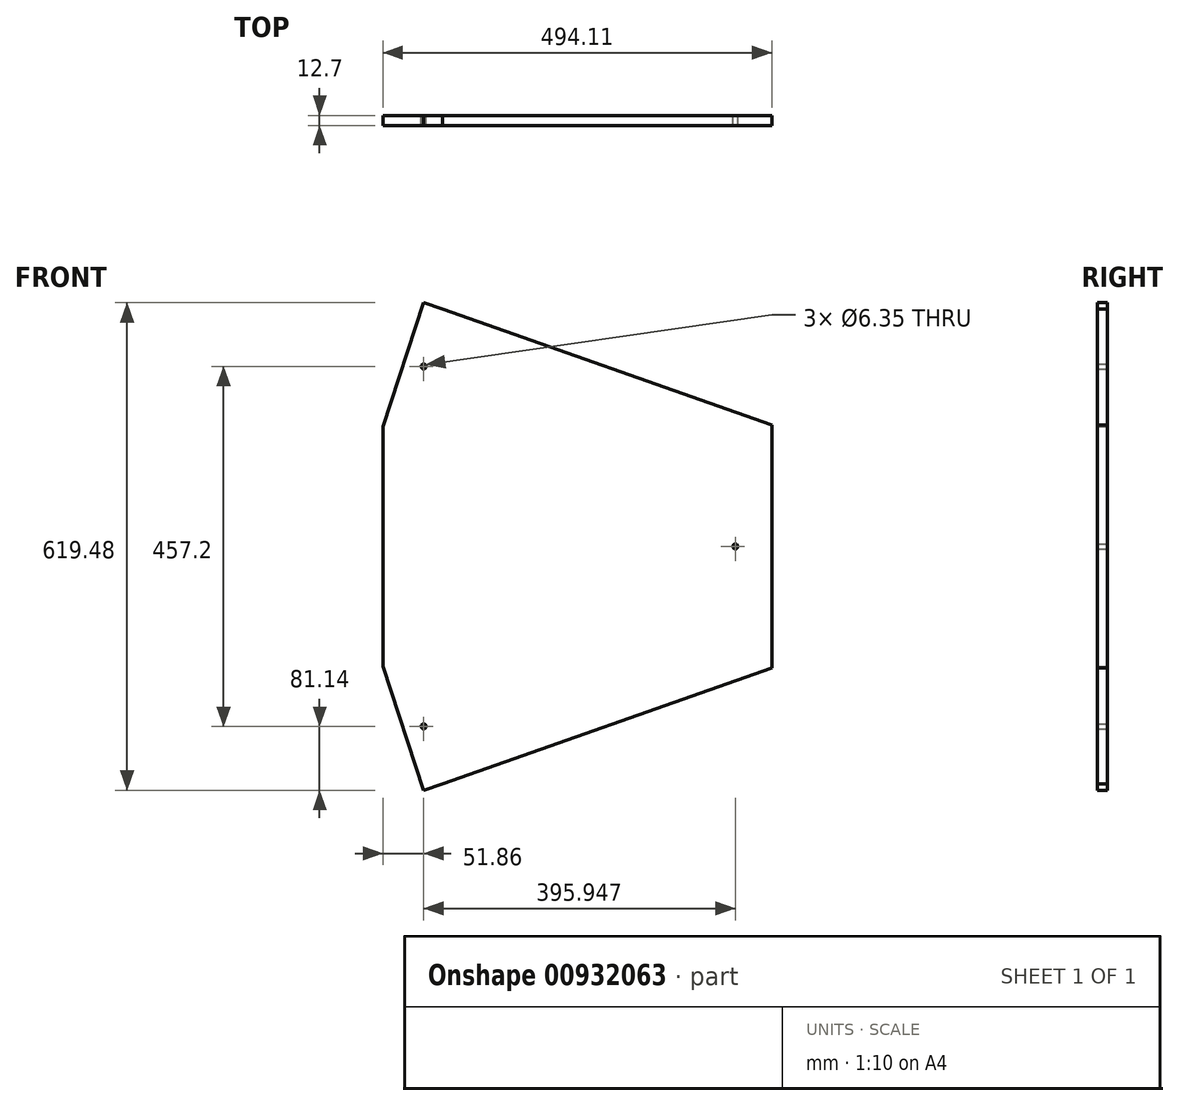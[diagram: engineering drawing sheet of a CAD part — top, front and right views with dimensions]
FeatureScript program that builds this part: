
annotation { "Feature Type Name" : "Feature", "Feature Type Description" : "" }
export const myFeature = defineFeature(function(context is Context, id is Id, definition is map)
    precondition{}
    {
        {
            var Q0;
            Q0=qCreatedBy(makeId("Front.planeOp"),FACE);
            var sketch = newSketch(context, id + "F0", { "sketchPlane" : qUnion([Q0])});
            skLineSegment(sketch, "E0", {"start": v(0, -228.6) * mm, "end": v(395.95, 0) * mm, "construction": true});
            skLineSegment(sketch, "E1", {"start": v(395.95, 0) * mm, "end": v(0, 228.6) * mm, "construction": true});
            skLineSegment(sketch, "E2", {"start": v(0, -228.6) * mm, "end": v(131.98, 0) * mm, "construction": true});
            skLineSegment(sketch, "E3", {"start": v(131.98, 0) * mm, "end": v(0, 228.6) * mm, "construction": true});
            skLineSegment(sketch, "E4", {"start": v(131.98, 0) * mm, "end": v(395.95, 0) * mm, "construction": true});
            skCircle(sketch, "E5", {"center": v(0, 228.6) * mm, "radius": 3.18 * mm});
            skCircle(sketch, "E6", {"center": v(0, -228.6) * mm, "radius": 3.18 * mm});
            skCircle(sketch, "E7", {"center": v(395.95, 0) * mm, "radius": 3.18 * mm});
            skLineSegment(sketch, "E8", {"start": v(0, 228.6) * mm, "end": v(0, 0) * mm, "construction": true});
            skLineSegment(sketch, "E9", {"start": v(0, 0) * mm, "end": v(0, -228.6) * mm, "construction": true});
            skLineSegment(sketch, "E10", {"start": v(-16.04, 179.94) * mm, "end": v(24.12, 301.79) * mm, "construction": true});
            skLineSegment(sketch, "E11", {"start": v(-16.04, -179.94) * mm, "end": v(24.12, -301.79) * mm, "construction": true});
            skLineSegment(sketch, "E12", {"start": v(0, 309.74) * mm, "end": v(-51.86, 152.4) * mm});
            skLineSegment(sketch, "E13", {"start": v(-51.86, -152.4) * mm, "end": v(0, -309.74) * mm});
            skLineSegment(sketch, "E14", {"start": v(0, 309.74) * mm, "end": v(24.12, 301.79) * mm});
            skLineSegment(sketch, "E15", {"start": v(0, -309.74) * mm, "end": v(24.12, -301.79) * mm});
            skLineSegment(sketch, "E16", {"start": v(24.12, -301.79) * mm, "end": v(442.25, -154.25) * mm});
            skLineSegment(sketch, "E17", {"start": v(442.25, -154.25) * mm, "end": v(442.25, 154.25) * mm});
            skLineSegment(sketch, "E18", {"start": v(442.25, 154.25) * mm, "end": v(24.12, 301.79) * mm});
            skPoint(sketch, "E19", {"position": v(442.25, 0) * mm});
            skLineSegment(sketch, "E20", {"start": v(-51.86, -152.4) * mm, "end": v(-51.86, 152.4) * mm});
            skPoint(sketch, "E21", {"position": v(-51.86, 0) * mm});
            skSolve(sketch);
        }
        {
            var Q0;
            Q0 = qSketchRegion(id + "F0", true);
            extrude(context, id + "F1", {"entities" : qUnion([Q0]), "depth" : 12.7 * mm, "offsetDistance" : 25.4 * mm});
        }
    });
